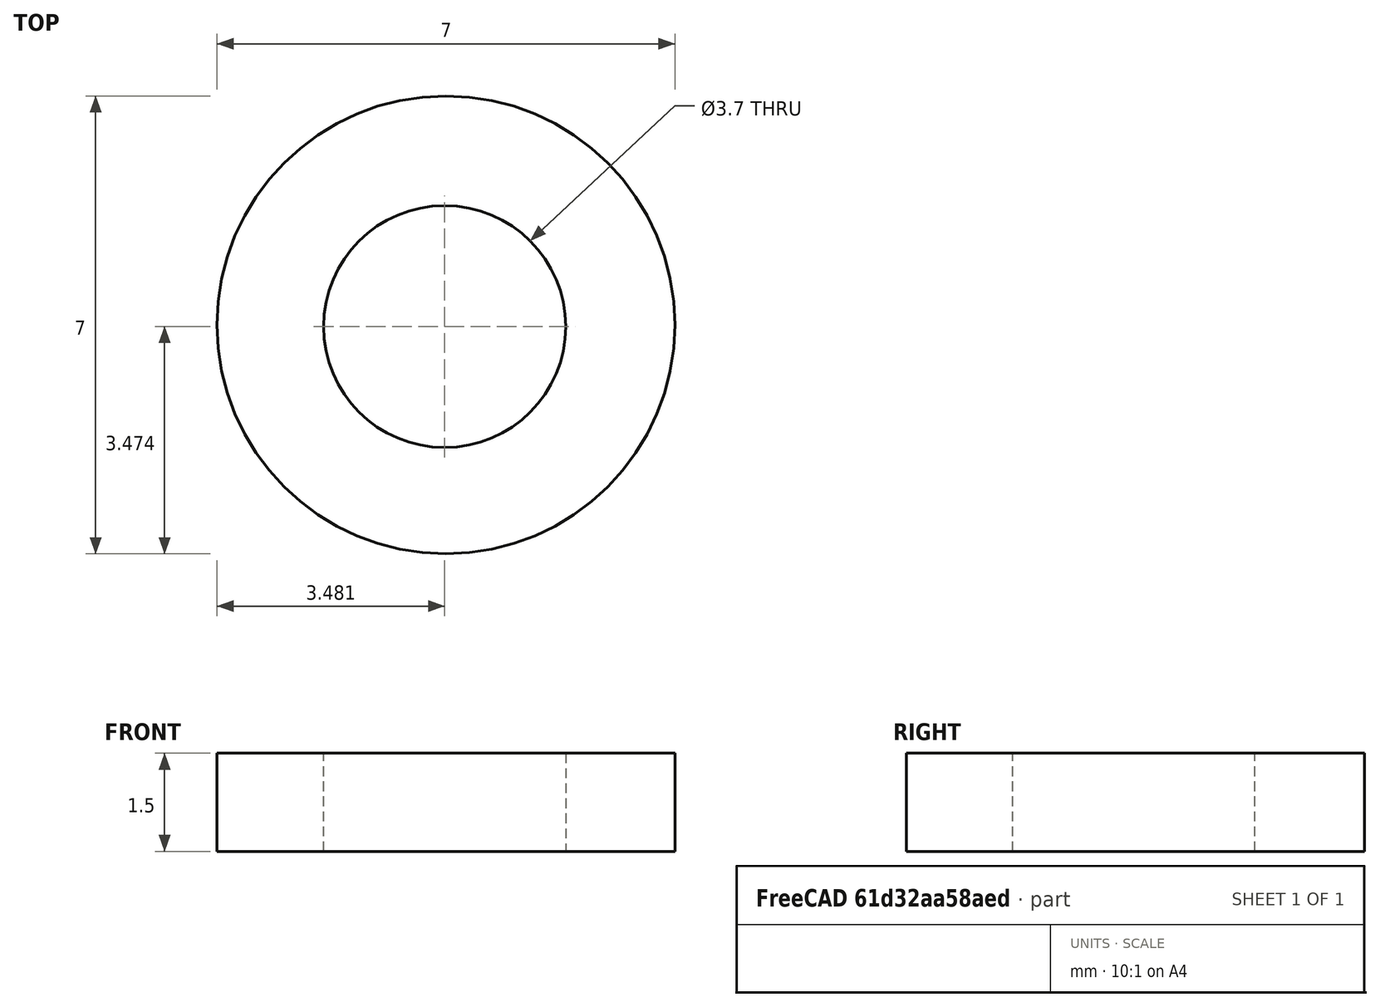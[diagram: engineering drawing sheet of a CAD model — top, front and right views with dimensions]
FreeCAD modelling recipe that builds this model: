
FCSTD DOCUMENT  (FreeCAD 0.19R19180 (Git))
Label: pcb_washer
License: All rights reserved
LicenseURL: http://en.wikipedia.org/wiki/All_rights_reserved
objects: Sketcher::SketchObject×2, PartDesign::Pad×1, PartDesign::Pocket×1, PartDesign::Body×1
note: 7 computed .brp shape members not serialized (recipe doc carries the construction recipe); baked Part::Feature solids carry a one-line shape summary decoded from their .brp

FEATURE [Sketcher::SketchObject] Sketch
  MapMode = 5
  Support = -> [XY_Plane]
  sketch-geometry (1):
    g0: Circle CenterX=0 CenterY=0 CenterZ=0 NormalX=0 NormalY=0 NormalZ=1 AngleXU=0 Radius=3.5
  constraints (2):
    c: Coincident(g0,g-1)
    c: Diameter(g0) = 7
FEATURE [PartDesign::Pad] Pad
  Length = 1.5
  Length2 = 100
  Profile = -> Sketch
  Type = 0
FEATURE [Sketcher::SketchObject] Sketch001
  MapMode = 5
  Placement = pos=(0,0,1.5) rot=(0,0,1;0rad)
  Support = -> [Pad]
  sketch-geometry (1):
    g0: Circle CenterX=-0.019309 CenterY=-0.026468 CenterZ=0 NormalX=0 NormalY=0 NormalZ=1 AngleXU=0 Radius=1.85
  constraints (1):
    c: Diameter(g0) = 3.7
FEATURE [PartDesign::Pocket] Pocket
  BaseFeature = -> Pad
  Length = 5
  Length2 = 100
  Profile = -> Sketch001
  Type = 0
FEATURE [PartDesign::Body] Body
  Group = -> [Sketch,Pad,Sketch001,Pocket]
  Origin = -> Origin
  Tip = -> Pocket
